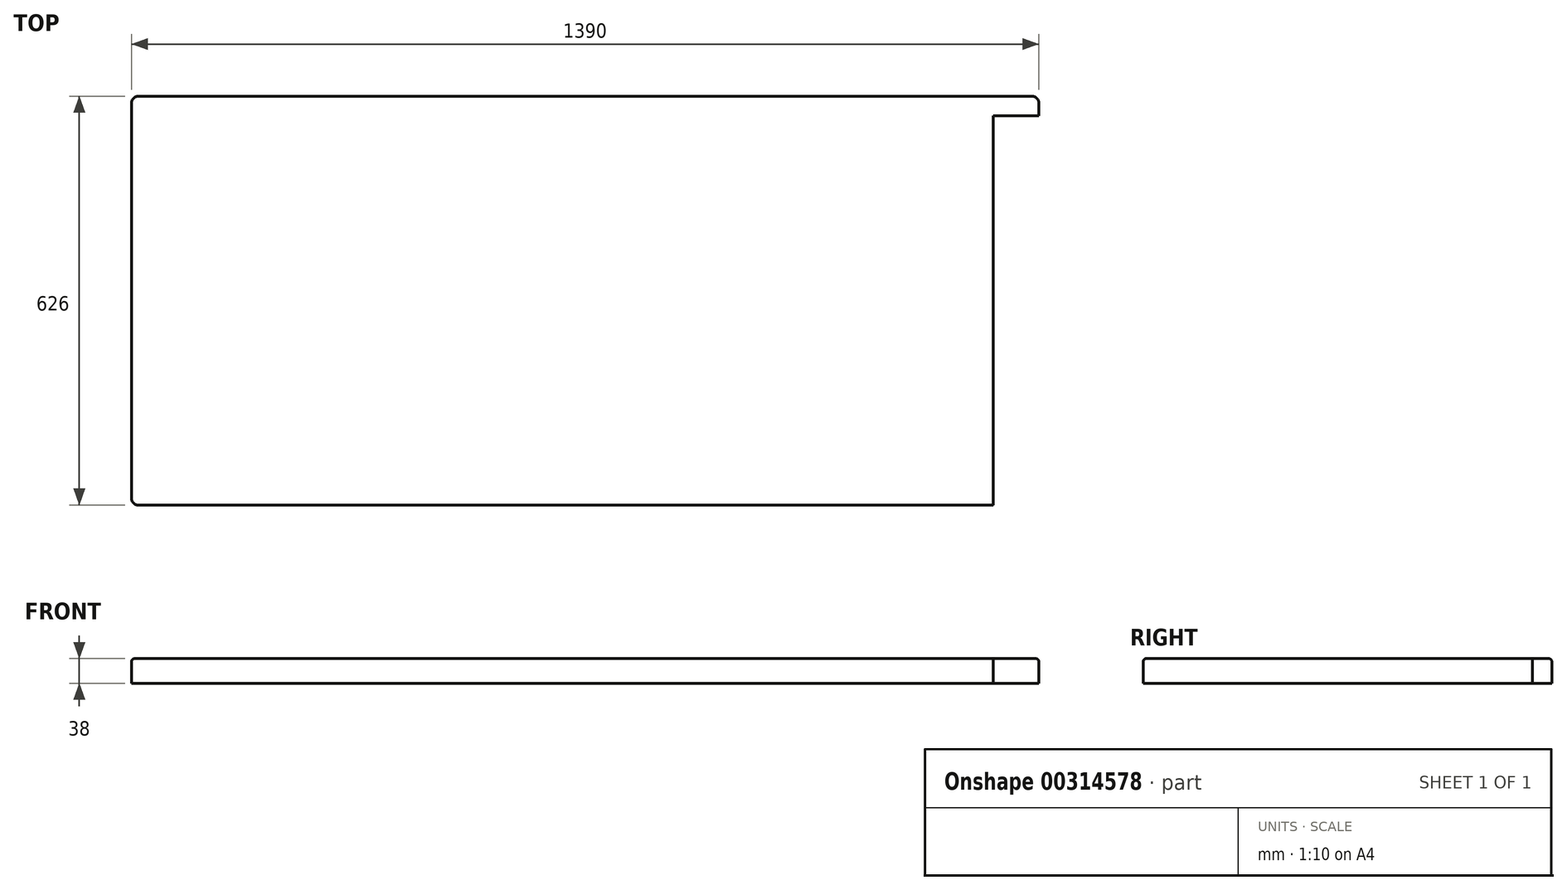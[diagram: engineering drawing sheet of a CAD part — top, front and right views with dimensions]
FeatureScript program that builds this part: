
annotation { "Feature Type Name" : "Feature", "Feature Type Description" : "" }
export const myFeature = defineFeature(function(context is Context, id is Id, definition is map)
    precondition{}
    {
        {
            var Q0;
            Q0=qCreatedBy(makeId("Top.planeOp"),FACE);
            var sketch = newSketch(context, id + "F0", { "sketchPlane" : qUnion([Q0])});
            skLineSegment(sketch, "E0", {"start": v(-640, 356.94) * mm, "end": v(730, 356.94) * mm});
            skLineSegment(sketch, "E1", {"start": v(740, 346.94) * mm, "end": v(740, 326.94) * mm});
            skLineSegment(sketch, "E2", {"start": v(740, 326.94) * mm, "end": v(670, 326.94) * mm});
            skLineSegment(sketch, "E3", {"start": v(670, 326.94) * mm, "end": v(670, -269.06) * mm});
            skLineSegment(sketch, "E4", {"start": v(670, -269.06) * mm, "end": v(-640, -269.06) * mm});
            skLineSegment(sketch, "E5", {"start": v(-650, -259.06) * mm, "end": v(-650, 346.94) * mm});
            skArc(sketch, "E6.filletArc", {"start": v(-640, 356.94) * mm, "mid": v(-647.07, 354.01) * mm, "end": v(-650, 346.94) * mm});
            skArc(sketch, "E7.filletArc", {"start": v(-650, -259.06) * mm, "mid": v(-647.07, -266.13) * mm, "end": v(-640, -269.06) * mm});
            skArc(sketch, "E8.filletArc", {"start": v(740, 346.94) * mm, "mid": v(737.07, 354.01) * mm, "end": v(730, 356.94) * mm});
            skSolve(sketch);
        }
        {
            var Q0;
            Q0=makeQuery(id+"F0.imprint","IMPRINT",FACE,{"disambiguationData":[TD([[makeQuery(id+"F0.imprint","IMPRINT",EDGE,{"derivedFrom":sQuery(id+"F0.wireOp",EDGE,"E0")}),-1.0]])]});
            extrude(context, id + "F1", {"entities" : qUnion([Q0]), "depth" : 38 * mm});
        }
        {
            var Q0;
            Q0=makeQuery(id+"F1.opExtrude","CAP_EDGE",EDGE,{"disambiguationData":[OSD([sQuery(id+"F0.wireOp",EDGE,"E5")])],"isStart":false});
            fillet(context, id + "F2", {"entities" : qUnion([Q0]), "radius" : 5 * mm, "tangentPropagation" : true, "allowEdgeOverflow" : false});
        }
    });
